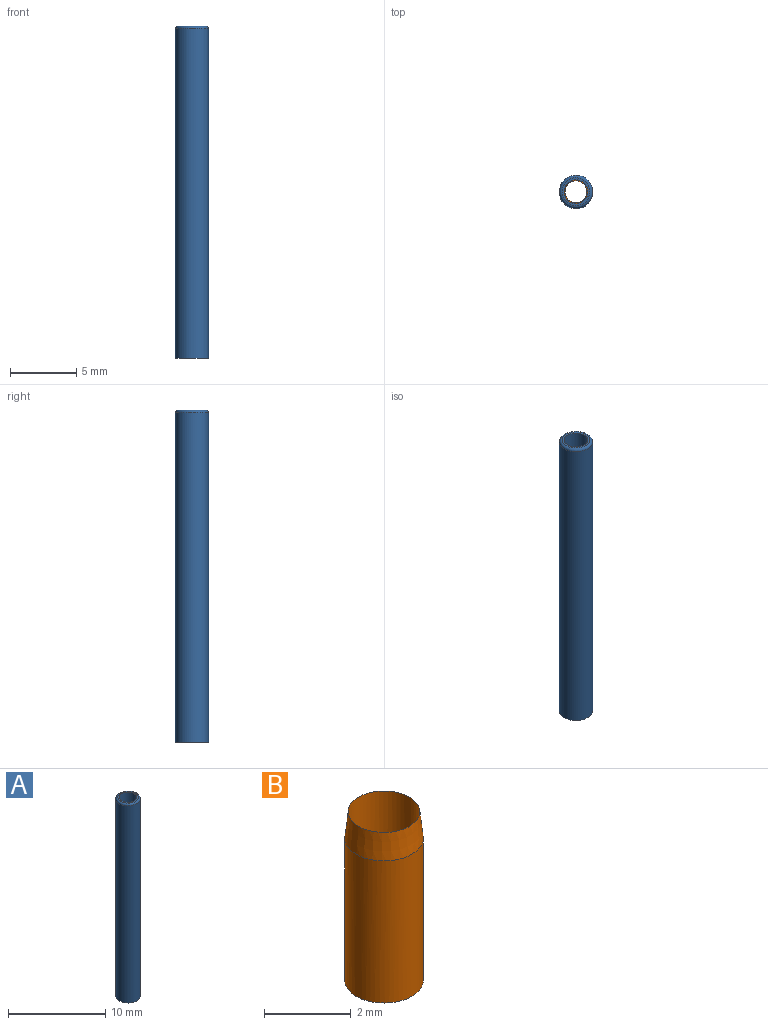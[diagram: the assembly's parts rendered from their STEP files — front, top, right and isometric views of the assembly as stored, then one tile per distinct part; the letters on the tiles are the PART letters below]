
ASSEMBLY  parts=2 mates=1
PART A: 5 faces, bbox 2.7x2.7x25 mm
  f0: cylinder r=0.9mm len=25mm, axis (0,0,-1), area 141.4mm2, adj f2,f3
  f1: cylinder r=1.25mm len=24.8mm, axis (0,0,-1), area 194.8mm2, adj f3,f4
  f2: plane 2.1x2.1mm, normal (0,0,1), area 0.9mm2, adj f0,f4
  f3: plane 2.5x2.5mm, normal (0,0,-1), area 2.4mm2, adj f0,f1
  f4: torus R=1.05mm, axis (0,0,1), area 2.3mm2, adj f1,f2
PART B: 4 faces, bbox 1.8x1.8x4.8 mm
  f0: cylinder r=0.82mm len=4.75mm, axis (0,0,-1), area 24.6mm2, adj f2,f3
  f1: cylinder r=0.9mm len=4mm, axis (0,0,-1), area 22.6mm2, adj f2,f3
  f2: plane 1.8x1.8mm, normal (0,0,-1), area 0.4mm2, adj f0,f1
  f3: cone r=0.8mm half-angle=5.7deg, axis (0,0,-1), area 4.1mm2, adj f0,f1
PLACE A t=(-1.66,5.75,-2.44)mm
PLACE B t=(-1.66,5.75,15.87)mm
MATE slider B.f1 <-> A.f1  axis (0,0,-1) through (-1.66,5.75,20.62)mm
